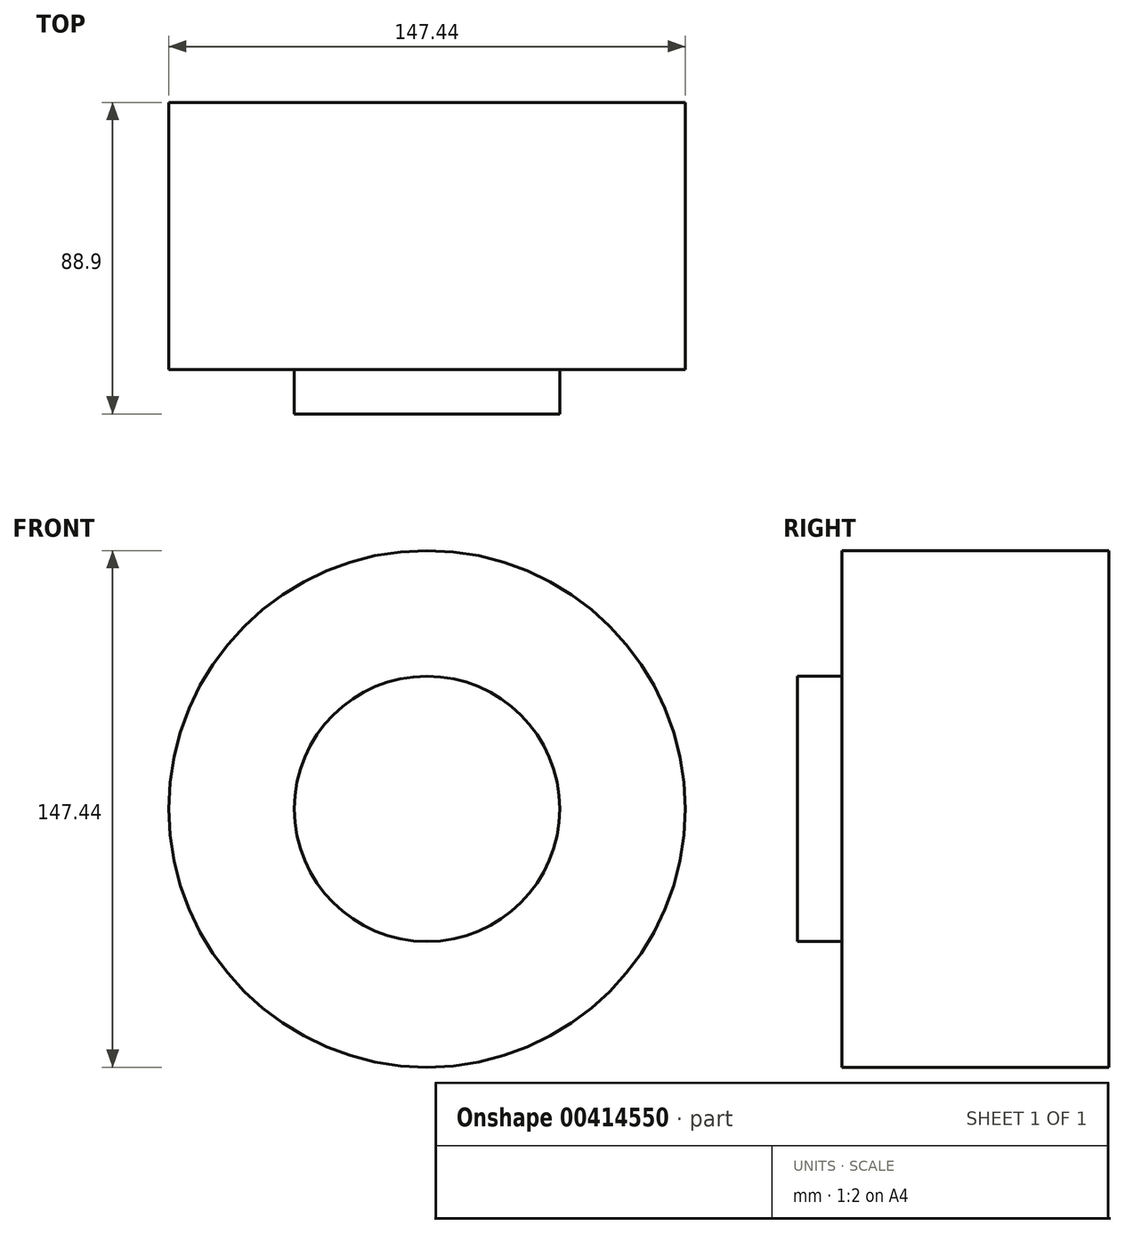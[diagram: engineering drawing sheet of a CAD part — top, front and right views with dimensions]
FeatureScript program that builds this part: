
annotation { "Feature Type Name" : "Feature", "Feature Type Description" : "" }
export const myFeature = defineFeature(function(context is Context, id is Id, definition is map)
    precondition{}
    {
        {
            var Q0;
            Q0=qCreatedBy(makeId("Front.planeOp"),FACE);
            var sketch = newSketch(context, id + "F0", { "sketchPlane" : qUnion([Q0])});
            skCircle(sketch, "E0", {"center": v(0, 0) * mm, "radius": 73.72 * mm});
            skSolve(sketch);
        }
        {
            var Q0;
            Q0 = qSketchRegion(id + "F0", true);
            extrude(context, id + "F1", {"entities" : qUnion([Q0]), "oppositeDirection" : true, "depth" : 76.2 * mm});
        }
        {
            var Q0;
            Q0=qCreatedBy(makeId("Front.planeOp"),FACE);
            var sketch = newSketch(context, id + "F2", { "sketchPlane" : qUnion([Q0])});
            skCircle(sketch, "E1", {"center": v(0, 0) * mm, "radius": 37.86 * mm});
            skSolve(sketch);
        }
        {
            var Q0;
            Q0 = qSketchRegion(id + "F2", true);
            extrude(context, id + "F3", {"entities" : qUnion([Q0]), "operationType" : NewBodyOperationType.ADD, "depth" : 12.7 * mm});
        }
    });
